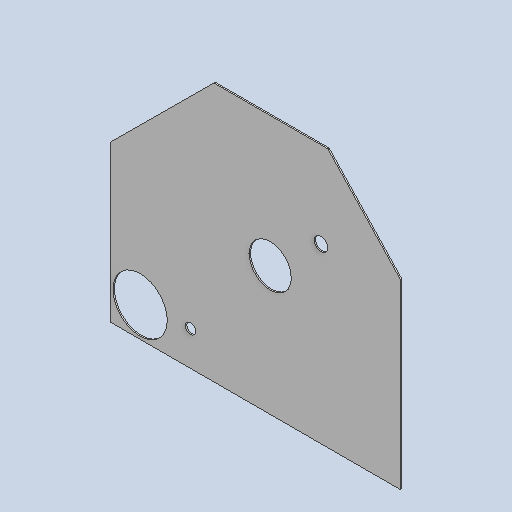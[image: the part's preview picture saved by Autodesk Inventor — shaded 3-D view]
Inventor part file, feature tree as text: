
AUTODESK INVENTOR PART (.ipt)
format: ipt  version: 2025 (Build 290162010, 162A)  size: 184,320 bytes
history: native  units: mm
features: extrude x2, sketch x1, other x1
ambient origin geometry x8: Origin, YZ Plane, XZ Plane, XY Plane, X Axis, Y Axis, Z Axis, Center Point
bodies: Solid1 (feature_tree)
feature tree (4):
  extrude  "Extrusion1"  Depth=10.0mm
  extrude  "Extrusion3"  Depth=10.0mm
  sketch  "Sketch3"  dims[d1=840.0mm d3=1150.0mm d11=390.0mm d12=1180.0mm d13=950.0mm d14=76.0mm d15=1910.0mm d16=255.0mm d17=220.0mm d18=401.0mm d19=220.0mm d21=1277.0mm d22=1554.635823mm d23=100.0mm d24=10.0mm d25=0.0mm d33=2140.0mm d34=494.0mm d37=10.0mm d38=0.0mm d45=310.0mm d47=5.0mm d48=80.0mm d49=372.0mm d51=780.0mm d52=1078.0mm]
  other  "Definition1"
